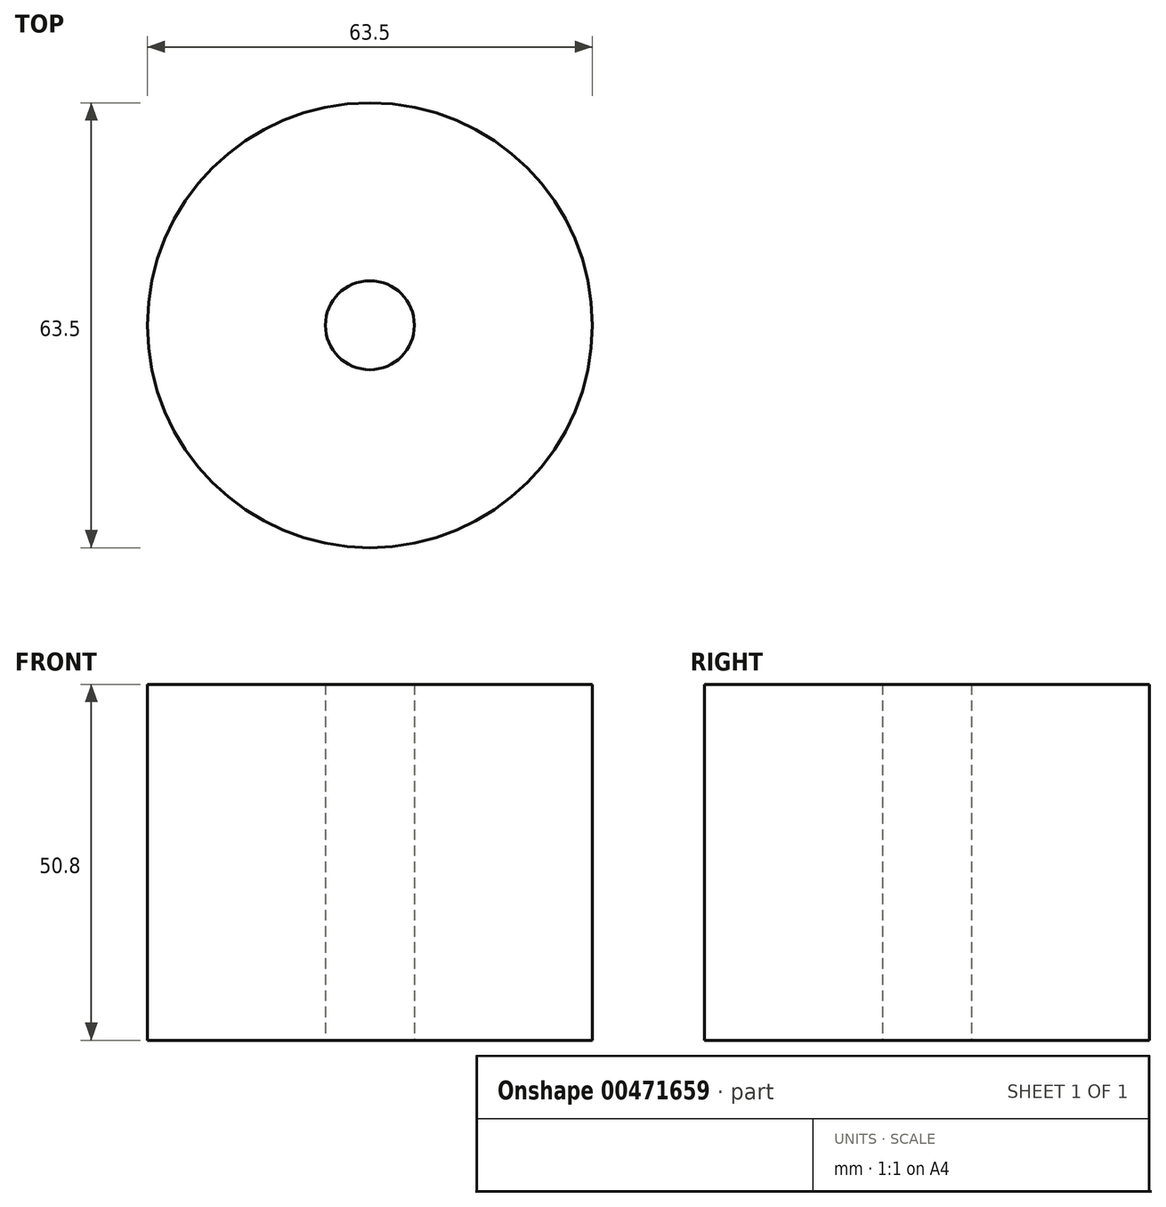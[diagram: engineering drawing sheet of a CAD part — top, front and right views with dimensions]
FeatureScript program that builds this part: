
annotation { "Feature Type Name" : "Feature", "Feature Type Description" : "" }
export const myFeature = defineFeature(function(context is Context, id is Id, definition is map)
    precondition{}
    {
        {
            var Q0;
            Q0=qCreatedBy(makeId("Front.planeOp"),FACE);
            var sketch = newSketch(context, id + "F0", { "sketchPlane" : qUnion([Q0])});
            skLineSegment(sketch, "E0", {"start": v(6.35, 63.5) * mm, "end": v(31.75, 63.5) * mm});
            skLineSegment(sketch, "E1", {"start": v(31.75, 63.5) * mm, "end": v(31.75, 12.7) * mm});
            skLineSegment(sketch, "E2", {"start": v(31.75, 12.7) * mm, "end": v(6.35, 12.7) * mm});
            skLineSegment(sketch, "E3", {"start": v(6.35, 12.7) * mm, "end": v(6.35, 63.5) * mm});
            skSolve(sketch);
        }
        {
            var Q0;
            Q0=qCreatedBy(makeId("Front.planeOp"),FACE);
            var sketch = newSketch(context, id + "F1", { "sketchPlane" : qUnion([Q0])});
            skLineSegment(sketch, "E4", {"start": v(0, 0) * mm, "end": v(0, 76.44) * mm});
            skSolve(sketch);
        }
        {
            var Q0;
            Q0 = qSketchRegion(id + "F0", true);
            var Q1;
            Q1=sQuery(id+"F1.wireOp",EDGE,"E4");
            revolve(context, id + "F2", {"entities" : qUnion([Q0]), "axis" : qUnion([Q1]), "revolveType" : RevolveType.FULL});
        }
    });
